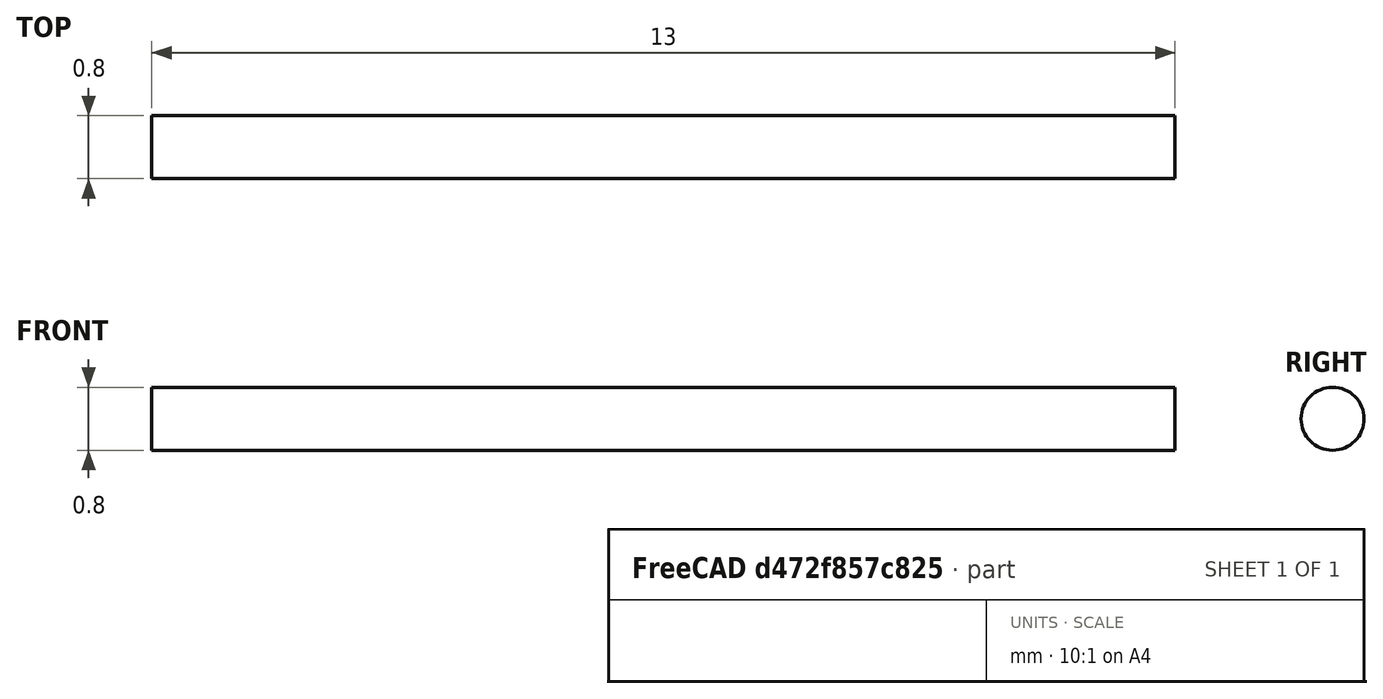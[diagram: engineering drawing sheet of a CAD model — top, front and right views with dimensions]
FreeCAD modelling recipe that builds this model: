
FCSTD DOCUMENT  (FreeCAD 1.0R39109 (Git))
Label: StepperMotor_8mm_i500212644_v2
License: All rights reserved
LicenseURL: https://en.wikipedia.org/wiki/All_rights_reserved
objects: Sketcher::SketchObject×2, PartDesign::Body×2, PartDesign::SubShapeBinder×1, PartDesign::Revolution×1
note: 10 computed .brp shape members not serialized (recipe doc carries the construction recipe); baked Part::Feature solids carry a one-line shape summary decoded from their .brp

FEATURE [Sketcher::SketchObject] Sketch  label="MasterSketch"
  ArcFitTolerance = 1e-06
  FullyConstrained = false
  MakeInternals = false
  MapMode = 5
  sketch-geometry (64):
    g0: LineSegment StartX=3.15 StartY=0.4 StartZ=0 EndX=-9.85 EndY=0.4 EndZ=0
    g1: LineSegment StartX=-3.25 StartY=4.1 StartZ=0 EndX=-4.25 EndY=4.1 EndZ=0
    g2: LineSegment StartX=-9.85 StartY=0.4 StartZ=0 EndX=-9.85 EndY=0 EndZ=0
    g3: LineSegment StartX=3.15 StartY=0.4 StartZ=0 EndX=3.15 EndY=0 EndZ=0
    g4: LineSegment StartX=-4.25 StartY=1.6 StartZ=0 EndX=-4.25 EndY=4.1 EndZ=0
    g5: LineSegment StartX=-4.25 StartY=2 StartZ=0 EndX=-4.65 EndY=2 EndZ=0
    g6: LineSegment StartX=-4.65 StartY=2 StartZ=0 EndX=-4.65 EndY=0.45 EndZ=0
    g7: LineSegment StartX=-4.65 StartY=0.45 StartZ=0 EndX=-3.05 EndY=0.45 EndZ=0
    g8: LineSegment StartX=-3.05 StartY=0.45 StartZ=0 EndX=-3.05 EndY=1.5 EndZ=0
    g9: LineSegment StartX=-3.05 StartY=1.5 StartZ=0 EndX=-4.25 EndY=1.5 EndZ=0
    g10: LineSegment StartX=-4.25 StartY=1.5 StartZ=0 EndX=-4.25 EndY=2 EndZ=0
    g11: LineSegment StartX=3.45 StartY=0 StartZ=0 EndX=3.45 EndY=3.9 EndZ=0
    g12: LineSegment StartX=3.45 StartY=3.9 StartZ=0 EndX=3.25 EndY=3.9 EndZ=0
    g13: LineSegment StartX=3.25 StartY=3.9 StartZ=0 EndX=3.25 EndY=0 EndZ=0
    g14: LineSegment StartX=-9.85 StartY=0.4 StartZ=0 EndX=-7.35 EndY=0.4 EndZ=0
    g15: LineSegment StartX=-7.35 StartY=0.4 StartZ=0 EndX=-7.35 EndY=1.15 EndZ=0
    g16: LineSegment StartX=-7.35 StartY=1.15 StartZ=0 EndX=-9.85 EndY=1.15 EndZ=0
    g17: LineSegment StartX=-9.85 StartY=1.15 StartZ=0 EndX=-9.85 EndY=0.4 EndZ=0
    g18: LineSegment StartX=-9.85 StartY=0 StartZ=0 EndX=3.15 EndY=0 EndZ=0
    g19: LineSegment StartX=3.25 StartY=0 StartZ=0 EndX=3.45 EndY=0 EndZ=0
    g20: LineSegment StartX=-0.547223 StartY=1.96354 StartZ=0 EndX=-0.547223 EndY=1.76354 EndZ=0
    g21: LineSegment StartX=-0.547223 StartY=1.76354 StartZ=0 EndX=-3.25 EndY=1.76354 EndZ=0
    g22: LineSegment StartX=-3.25 StartY=1.76354 StartZ=0 EndX=-3.25 EndY=4 EndZ=0
    g23: LineSegment StartX=-3.25 StartY=4 StartZ=0 EndX=0 EndY=4 EndZ=0
    g24: LineSegment StartX=0 StartY=4 StartZ=0 EndX=3.25 EndY=4 EndZ=0
    g25: LineSegment StartX=3.25 StartY=4 StartZ=0 EndX=3.25 EndY=1.76354 EndZ=0
    g26: LineSegment StartX=3.25 StartY=1.76354 StartZ=0 EndX=0.547223 EndY=1.76354 EndZ=0
    g27: LineSegment StartX=0.547223 StartY=1.76354 StartZ=0 EndX=0.547223 EndY=1.96354 EndZ=0
    g28: LineSegment StartX=0.547223 StartY=1.96354 StartZ=0 EndX=3.05 EndY=1.96354 EndZ=0
    g29: LineSegment StartX=3.05 StartY=1.96354 StartZ=0 EndX=3.05 EndY=3.8 EndZ=0
    g30: LineSegment StartX=3.05 StartY=3.8 StartZ=0 EndX=0 EndY=3.8 EndZ=0
    g31: LineSegment StartX=0 StartY=3.8 StartZ=0 EndX=-3.05 EndY=3.8 EndZ=0
    g32: LineSegment StartX=-3.05 StartY=3.8 StartZ=0 EndX=-3.05 EndY=1.96354 EndZ=0
    g33: LineSegment StartX=-3.05 StartY=1.96354 StartZ=0 EndX=-0.547223 EndY=1.96354 EndZ=0
    g34: LineSegment [constr] StartX=0 StartY=3.8 StartZ=0 EndX=0 EndY=4 EndZ=0
    g35: LineSegment [constr] StartX=3.05 StartY=3.8 StartZ=0 EndX=3.25 EndY=3.8 EndZ=0
    g36: LineSegment StartX=-4.25 StartY=1.6 StartZ=0 EndX=-3.25 EndY=1.6 EndZ=0
    g37: LineSegment StartX=-3.25 StartY=1.6 StartZ=0 EndX=-3.25 EndY=4.1 EndZ=0
    g38: LineSegment [constr] StartX=-3.25 StartY=3.8 StartZ=0 EndX=-3.05 EndY=3.8 EndZ=0
    g39: LineSegment StartX=-2.83215 StartY=3.37089 StartZ=0 EndX=-2.83215 EndY=2.45148 EndZ=0
    g40: LineSegment StartX=-2.55591 StartY=2.17524 StartZ=0 EndX=-0.807353 EndY=2.17524 EndZ=0
    g41: LineSegment StartX=-0.531117 StartY=2.45148 StartZ=0 EndX=-0.531117 EndY=3.37089 EndZ=0
    g42: LineSegment StartX=-0.807353 StartY=3.64713 StartZ=0 EndX=-2.55591 EndY=3.64713 EndZ=0
    g43: ArcOfCircle CenterX=-2.55591 CenterY=3.37089 CenterZ=0 NormalX=0 NormalY=0 NormalZ=1 AngleXU=0 Radius=0.276236 StartAngle=1.5708 EndAngle=3.14159
    g44: ArcOfCircle CenterX=-2.55591 CenterY=2.45148 CenterZ=0 NormalX=0 NormalY=0 NormalZ=1 AngleXU=0 Radius=0.276236 StartAngle=3.14159 EndAngle=4.71239
    g45: ArcOfCircle CenterX=-0.807353 CenterY=2.45148 CenterZ=0 NormalX=0 NormalY=0 NormalZ=1 AngleXU=0 Radius=0.276236 StartAngle=4.71239 EndAngle=6.28319
    g46: ArcOfCircle CenterX=-0.807353 CenterY=3.37089 CenterZ=0 NormalX=0 NormalY=0 NormalZ=1 AngleXU=0 Radius=0.276236 StartAngle=4e-16 EndAngle=1.5708
    g47: GeomPoint [constr] X=-2.83215 Y=3.64713 Z=0
    g48: GeomPoint [constr] X=-0.531117 Y=2.17524 Z=0
    g49: LineSegment StartX=-2.88425 StartY=0.4 StartZ=0 EndX=2.88425 EndY=0.4 EndZ=0
    g50: LineSegment StartX=2.88425 StartY=0.4 StartZ=0 EndX=2.88425 EndY=1.6 EndZ=0
    g51: LineSegment StartX=2.88425 StartY=1.6 StartZ=0 EndX=-2.88425 EndY=1.6 EndZ=0
    g52: LineSegment StartX=-2.88425 StartY=1.6 StartZ=0 EndX=-2.88425 EndY=0.4 EndZ=0
    g53: LineSegment StartX=0.531117 StartY=3.37089 StartZ=0 EndX=0.531117 EndY=2.45148 EndZ=0
    g54: LineSegment StartX=0.807353 StartY=2.17524 StartZ=0 EndX=2.55591 EndY=2.17524 EndZ=0
    g55: LineSegment StartX=2.83215 StartY=2.45148 StartZ=0 EndX=2.83215 EndY=3.37089 EndZ=0
    g56: LineSegment StartX=2.55591 StartY=3.64713 StartZ=0 EndX=0.807353 EndY=3.64713 EndZ=0
    g57: ArcOfCircle CenterX=0.807353 CenterY=3.37089 CenterZ=0 NormalX=0 NormalY=0 NormalZ=1 AngleXU=0 Radius=0.276236 StartAngle=1.5708 EndAngle=3.14159
    g58: ArcOfCircle CenterX=0.807353 CenterY=2.45148 CenterZ=0 NormalX=0 NormalY=0 NormalZ=1 AngleXU=0 Radius=0.276236 StartAngle=3.14159 EndAngle=4.71239
    g59: ArcOfCircle CenterX=2.55591 CenterY=2.45148 CenterZ=0 NormalX=0 NormalY=0 NormalZ=1 AngleXU=0 Radius=0.276236 StartAngle=4.71239 EndAngle=6.28319
    g60: ArcOfCircle CenterX=2.55591 CenterY=3.37089 CenterZ=0 NormalX=0 NormalY=0 NormalZ=1 AngleXU=0 Radius=0.276236 StartAngle=0 EndAngle=1.5708
    g61: GeomPoint [constr] X=0.531117 Y=3.64713 Z=0
    g62: GeomPoint [constr] X=2.83215 Y=2.17524 Z=0
    g63: LineSegment StartX=-9.85 StartY=0.4 StartZ=0 EndX=-7.35 EndY=0.4 EndZ=0
  constraints (160):
    c: Horizontal(g0)
    c: Horizontal(g1)
    c: Coincident(g2,g0)
    c: PointOnObject(g2,g-1)
    c: Vertical(g2)
    c: Coincident(g3,g0)
    c: PointOnObject(g3,g-1)
    c: Vertical(g3)
    c: Coincident(g4,g1)
    c: Vertical(g4)
    c: PointOnObject(g5,g4)
    c: Horizontal(g5)
    c: Coincident(g6,g5)
    c: Vertical(g6)
    c: Coincident(g8,g7)
    c: Vertical(g8)
    c: Coincident(g9,g8)
    c: Horizontal(g9)
    c: Coincident(g10,g9)
    c: Coincident(g10,g5)
    c: Vertical(g10)
    c: Coincident(g11,g12)
    c: Coincident(g12,g13)
    c: Horizontal(g12)
    c: Vertical(g11)
    c: PointOnObject(g13,g-1)
    c: Coincident(g14,g15)
    c: Coincident(g15,g16)
    c: Coincident(g16,g17)
    c: Coincident(g17,g14)
    c: Horizontal(g14)
    c: Horizontal(g16)
    c: Vertical(g15)
    c: Vertical(g17)
    c: Coincident(g14,g0)
    c: Coincident(g18,g2)
    c: Coincident(g18,g3)
    c: Coincident(g19,g13)
    c: Coincident(g19,g11)
    c: Horizontal(g19)
    c: DistanceX(g1,g1) = 1  'MountingPlateThickness'
    c: DistanceX(g12,g12) = 0.2  'EndCapThickness'
    c: DistanceY(g11,g11) = 3.9  'EndCap Radius'
    c: DistanceX(g5,g5) = 0.4  'BushingFlangeThickness'
    c: DistanceX(g16,g16) = 2.5  'GearLength'
    c: Horizontal(g7)
    c: Coincident(g7,g6)
    c: Distance(g18,g0) = 0.4  'ShaftRadius'
    c: Vertical(g13)
    c: DistanceY(g2,g16) = 1.15  'GearRadius'
    c: Distance(g8,g18) = 1.5  'BushingInnerRadius'
    c: DistanceY(g-1,g1) = 4.1  'MountingPlateRadius'
    c: Distance(g6,g0) = 0.05  'BushingShaftClearance'
    c: Distance(g5,g18) = 2  'BushingFlangeRadius'
    c: DistanceX(g3,g13) = 0.1  'ShaftEndCapClearance'
    c: DistanceX(g2,g11) = 13.3  'TotalLength'
    c: DistanceX(g6,g7) = 1.6  'BushingCollarDepth'
    c: Vertical(g20)
    c: Coincident(g20,g21)
    c: Coincident(g21,g22)
    c: Coincident(g22,g23)
    c: PointOnObject(g23,g-2)
    c: Horizontal(g23)
    c: Coincident(g23,g24)
    c: Horizontal(g24)
    c: Coincident(g24,g25)
    c: Coincident(g25,g26)
    c: Coincident(g26,g27)
    c: Vertical(g27)
    c: Coincident(g27,g28)
    c: Horizontal(g28)
    c: Coincident(g28,g29)
    c: Vertical(g29)
    c: Coincident(g29,g30)
    c: PointOnObject(g30,g-2)
    c: Horizontal(g30)
    c: Coincident(g30,g31)
    c: Horizontal(g31)
    c: Coincident(g31,g32)
    c: Vertical(g32)
    c: Coincident(g32,g33)
    c: Coincident(g33,g20)
    c: Horizontal(g33)
    c: Coincident(g34,g30)
    c: Coincident(g34,g23)
    c: Coincident(g35,g29)
    c: PointOnObject(g35,g25)
    c: Horizontal(g35)
    c: Coincident(g4,g36)
    c: Horizontal(g36)
    c: Coincident(g36,g37)
    c: Coincident(g37,g1)
    c: Vertical(g37)
    c: PointOnObject(g38,g22)
    c: Coincident(g38,g31)
    c: Horizontal(g38)
    c: Equal(g38,g34)
    c: Equal(g34,g35)
    c: Distance(g34,g34) = 0.2  'BodyCanThickness'
    c: Equal(g34,g20)
    c: Equal(g20,g27)
    c: Tangent(g21,g26)
    c: Symmetric(g20,g26,g-2)
    c: Symmetric(g21,g25,g-2)
    c: Distance(g-1,g23) = 4  'BodyCanRadius'
    c: Tangent(g37,g22)
    c: Tangent(g25,g13)
    c: DistanceX(g23,g23) = 3.25  'BodyCanHalfLength'
    c: Distance(g9,g36) = 0.1  'BushingMountingPlateClearance'
    c: Tangent(g39,g43) = -1.5708
    c: Tangent(g39,g44) = -1.5708
    c: Tangent(g40,g44) = -1.5708
    c: Tangent(g40,g45) = -1.5708
    c: Tangent(g41,g45) = -1.5708
    c: Tangent(g41,g46) = -1.5708
    c: Tangent(g42,g46) = -1.5708
    c: Tangent(g42,g43) = -1.5708
    c: Vertical(g39)
    c: Vertical(g41)
    c: Horizontal(g40)
    c: Horizontal(g42)
    c: Equal(g43,g44)
    c: Equal(g44,g45)
    c: Equal(g45,g46)
    c: PointOnObject(g47,g39)
    c: PointOnObject(g47,g42)
    c: PointOnObject(g48,g40)
    c: PointOnObject(g48,g41)
    c: Coincident(g49,g50)
    c: Coincident(g50,g51)
    c: Coincident(g51,g52)
    c: Coincident(g52,g49)
    c: Horizontal(g49)
    c: Vertical(g50)
    c: Vertical(g52)
    c: PointOnObject(g49,g0)
    c: Distance(g-1,g51) = 1.6  'MagnetRadius'
    c: Symmetric(g51,g50,g-2)
    c: Tangent(g53,g57) = -1.5708
    c: Tangent(g53,g58) = -1.5708
    c: Tangent(g54,g58) = -1.5708
    c: Tangent(g54,g59) = -1.5708
    c: Tangent(g55,g59) = -1.5708
    c: Tangent(g55,g60) = -1.5708
    c: Tangent(g56,g60) = -1.5708
    c: Tangent(g56,g57) = -1.5708
    c: Vertical(g53)
    c: Vertical(g55)
    c: Equal(g57,g58)
    c: Equal(g58,g59)
    c: PointOnObject(g61,g53)
    c: PointOnObject(g61,g56)
    c: PointOnObject(g62,g54)
    c: PointOnObject(g62,g55)
    c: Tangent(g40,g54)
    c: Tangent(g56,g42)
    c: Symmetric(g41,g53,g-2)
    c: Symmetric(g55,g39,g-2)
    c: Coincident(g63,g0)
    c: Coincident(g63,g14)
FEATURE [Sketcher::SketchObject] Sketch001
  ArcFitTolerance = 1e-06
  AttachmentSupport = -> [XY_Plane]
  FullyConstrained = true
  MakeInternals = false
  MapMode = 5
FEATURE [PartDesign::SubShapeBinder] Binder
  BindCopyOnChange = 0
  BindMode = 0
  ClaimChildren = false
  Context = -> Body [Binder.]
  Fuse = false
  MakeFace = true
  OffsetFill = false
  OffsetIntersection = false
  OffsetJoinType = 0
  OffsetOpenResult = false
  PartialLoad = false
  Refine = true
  Relative = true
  Support = -> [Sketch[Edge1,Edge7,Edge8,Edge9]]
  _Version = 2
FEATURE [PartDesign::Revolution] Revolution
  Angle = 360
  Angle2 = 60
  Axis = (1,0,0)
  Base = (0,0,0)
  Profile = -> Binder
  ReferenceAxis = -> X_Axis
  Refine = true
  Suppressed = false
  Type = 0
FEATURE [PartDesign::Body] Body  label="Shaft"
  AllowCompound = false
  Group = -> [Sketch001,Binder,Revolution]
  Origin = -> Origin
  Tip = -> Revolution
FEATURE [PartDesign::Body] Body001  label="Body"
  AllowCompound = false
  Origin = -> Origin001
